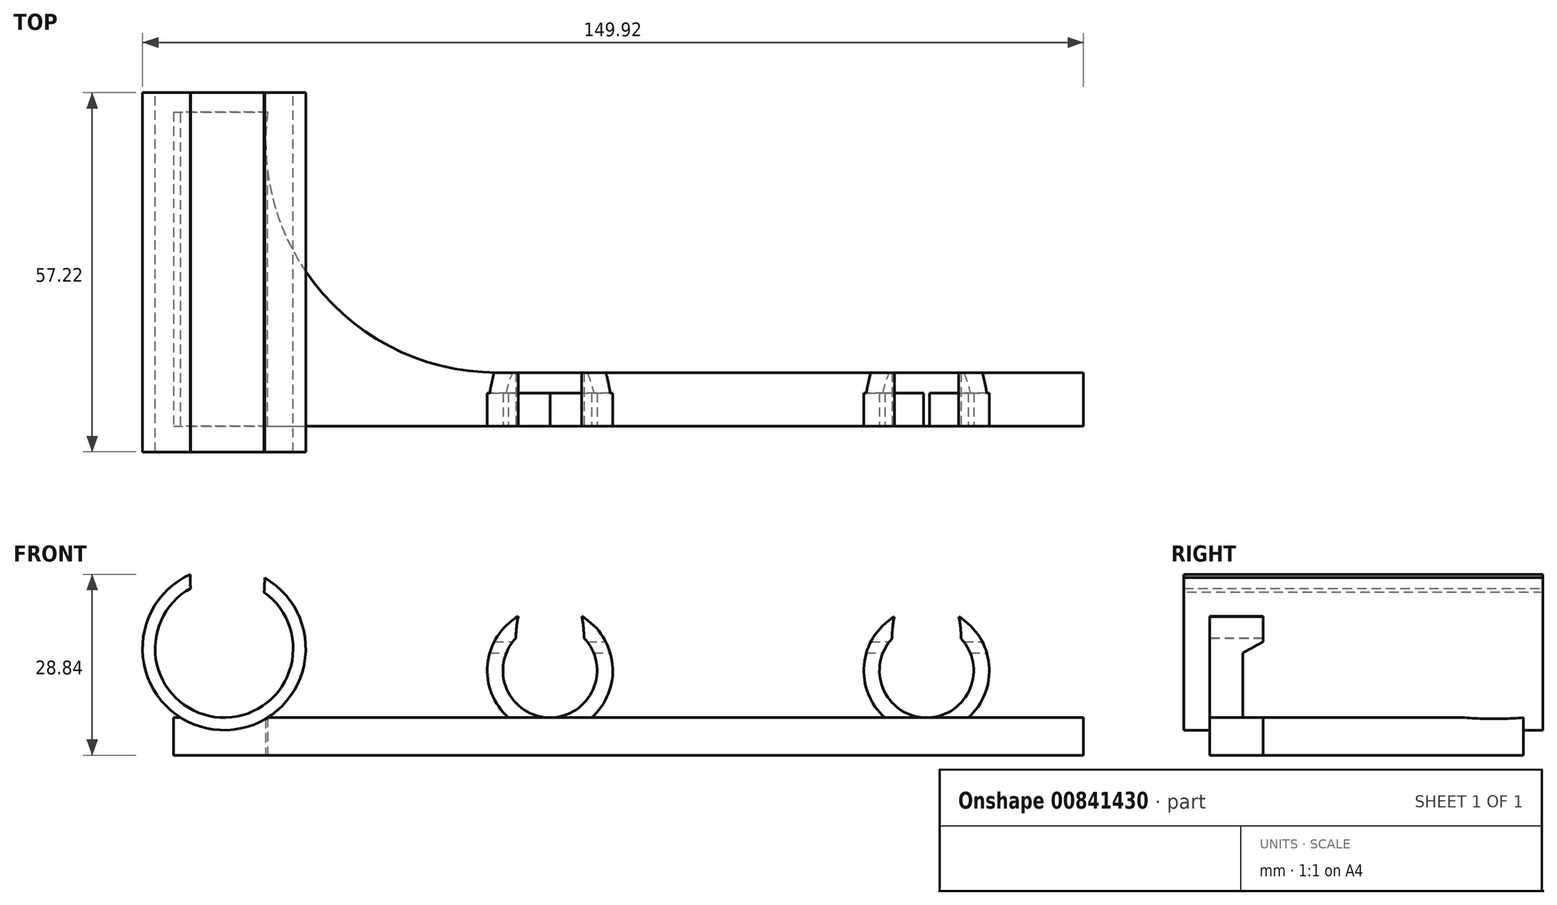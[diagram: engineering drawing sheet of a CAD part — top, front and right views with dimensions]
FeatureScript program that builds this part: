
annotation { "Feature Type Name" : "Feature", "Feature Type Description" : "" }
export const myFeature = defineFeature(function(context is Context, id is Id, definition is map)
    precondition{}
    {
        {
            var Q0;
            Q0=qCreatedBy(makeId("Top.planeOp"),FACE);
            var sketch = newSketch(context, id + "F0", { "sketchPlane" : qUnion([Q0])});
            skLineSegment(sketch, "E0", {"start": v(-14, 18.17) * mm, "end": v(-14, -31.83) * mm});
            skLineSegment(sketch, "E1", {"start": v(-14, -31.83) * mm, "end": v(131, -31.83) * mm});
            skLineSegment(sketch, "E2", {"start": v(131, -31.83) * mm, "end": v(131, -23.3) * mm});
            skLineSegment(sketch, "E3", {"start": v(131, -23.3) * mm, "end": v(37.51, -23.3) * mm});
            skLineSegment(sketch, "E4", {"start": v(-14, 18.17) * mm, "end": v(1, 18.17) * mm});
            skArc(sketch, "E5", {"start": v(1, 18.17) * mm, "mid": v(9.88, -10.82) * mm, "end": v(37.51, -23.3) * mm});
            skSolve(sketch);
        }
        {
            var Q0;
            Q0=makeQuery(id+"F0.imprint","IMPRINT",FACE,{"disambiguationData":[TD([[makeQuery(id+"F0.imprint","IMPRINT",EDGE,{"derivedFrom":sQuery(id+"F0.wireOp",EDGE,"E0")}),1.0]])]});
            extrude(context, id + "F1", {"entities" : qUnion([Q0]), "depth" : 5 * mm, "offsetDistance" : 25 * mm, "hasSecondDirection" : true, "secondDirectionOppositeDirection" : true, "secondDirectionDepth" : 1 * mm});
        }
        {
            var Q0;
            Q0=qCreatedBy(makeId("Front.planeOp"),FACE);
            var sketch = newSketch(context, id + "F2", { "sketchPlane" : qUnion([Q0])});
            skCircle(sketch, "E6", {"center": v(-5.92, 16) * mm, "radius": 11 * mm});
            skCircle(sketch, "E7", {"center": v(-5.92, 16) * mm, "radius": 13 * mm});
            skEllipse(sketch, "E8", {"center": v(-5.38, 26.99) * mm, "majorRadius": 11.85 * mm, "minorRadius": 5.92 * mm, "majorAxis": v(0, 1)});
            skSolve(sketch);
        }
        {
            var Q0;
            {var subQ0=sQuery(id+"F2.wireOp",EDGE,"E8");var subQ1=sQuery(id+"F2.wireOp",EDGE,"E6");var subQ2=makeQuery(id+"F2.imprint","INTERSECT",VERTEX,{"disambiguationData":[OD(0.0)],"derivedFrom":[subQ1,subQ0]});Q0=makeQuery(id+"F2.imprint","IMPRINT",FACE,{"disambiguationData":[TD([[makeQuery(id+"F2.imprint","IMPRINT",EDGE,{"disambiguationData":[TD([[subQ2,-1.0]])],"derivedFrom":subQ1}),-1.0]])]});}
            extrude(context, id + "F3", {"entities" : qUnion([Q0]), "operationType" : NewBodyOperationType.ADD, "depth" : 35.94 * mm, "offsetDistance" : 25 * mm, "hasSecondDirection" : true, "secondDirectionOppositeDirection" : true, "secondDirectionDepth" : 21.28 * mm});
        }
        {
            var Q0;
            Q0=makeQuery(id+"F1.opExtrude","SWEPT_FACE",FACE,{"disambiguationData":[OSD([sQuery(id+"F0.wireOp",EDGE,"E1")])]});
            var sketch = newSketch(context, id + "F4", { "sketchPlane" : qUnion([Q0])});
            skCircle(sketch, "E9", {"center": v(46, 12.5) * mm, "radius": 7.5 * mm});
            skCircle(sketch, "E10", {"center": v(106, 12.49) * mm, "radius": 7.5 * mm});
            skCircle(sketch, "E11", {"center": v(46, 12.5) * mm, "radius": 10 * mm});
            skCircle(sketch, "E12", {"center": v(106, 12.49) * mm, "radius": 10 * mm});
            skEllipse(sketch, "E13", {"center": v(106, 17.49) * mm, "majorRadius": 10 * mm, "minorRadius": 5.5 * mm, "majorAxis": v(0, 1)});
            skEllipse(sketch, "E14", {"center": v(46, 17.5) * mm, "majorRadius": 10 * mm, "minorRadius": 5.43 * mm, "majorAxis": v(0, 1)});
            skSolve(sketch);
        }
        {
            var Q0;
            {var subQ0=sQuery(id+"F4.wireOp",EDGE,"E14");var subQ1=sQuery(id+"F4.wireOp",EDGE,"E9");var subQ2=makeQuery(id+"F4.imprint","INTERSECT",VERTEX,{"disambiguationData":[OD(1.0)],"derivedFrom":[subQ1,subQ0]});Q0=makeQuery(id+"F4.imprint","IMPRINT",FACE,{"disambiguationData":[TD([[makeQuery(id+"F4.imprint","IMPRINT",EDGE,{"disambiguationData":[TD([[subQ2,1.0]])],"derivedFrom":subQ1}),-1.0]])]});}
            var Q1;
            {var subQ0=sQuery(id+"F4.wireOp",EDGE,"E14");var subQ1=sQuery(id+"F4.wireOp",EDGE,"E9");var subQ2=makeQuery(id+"F4.imprint","INTERSECT",VERTEX,{"disambiguationData":[OD(0.0)],"derivedFrom":[subQ1,subQ0]});Q1=makeQuery(id+"F4.imprint","IMPRINT",FACE,{"disambiguationData":[TD([[makeQuery(id+"F4.imprint","IMPRINT",EDGE,{"disambiguationData":[TD([[subQ2,-1.0]])],"derivedFrom":subQ1}),-1.0]])]});}
            var Q2;
            {var subQ0=sQuery(id+"F4.wireOp",EDGE,"E13");var subQ1=sQuery(id+"F4.wireOp",EDGE,"E10");var subQ2=makeQuery(id+"F4.imprint","INTERSECT",VERTEX,{"disambiguationData":[OD(0.0)],"derivedFrom":[subQ1,subQ0]});Q2=makeQuery(id+"F4.imprint","IMPRINT",FACE,{"disambiguationData":[TD([[makeQuery(id+"F4.imprint","IMPRINT",EDGE,{"disambiguationData":[TD([[subQ2,-1.0]])],"derivedFrom":subQ1}),-1.0]])]});}
            var Q3;
            {var subQ0=sQuery(id+"F4.wireOp",EDGE,"E13");var subQ1=sQuery(id+"F4.wireOp",EDGE,"E10");var subQ2=makeQuery(id+"F4.imprint","INTERSECT",VERTEX,{"disambiguationData":[OD(1.0)],"derivedFrom":[subQ1,subQ0]});Q3=makeQuery(id+"F4.imprint","IMPRINT",FACE,{"disambiguationData":[TD([[makeQuery(id+"F4.imprint","IMPRINT",EDGE,{"disambiguationData":[TD([[subQ2,1.0]])],"derivedFrom":subQ1}),-1.0]])]});}
            extrude(context, id + "F5", {"entities" : qUnion([Q0, Q1, Q2, Q3]), "oppositeDirection" : true, "depth" : 8.5 * mm, "offsetDistance" : 25 * mm});
        }
        {
            var Q0;
            Q0=makeQuery(id+"F1.opExtrude","SWEPT_FACE",FACE,{"disambiguationData":[OSD([sQuery(id+"F0.wireOp",EDGE,"E2")])]});
            var sketch = newSketch(context, id + "F6", { "sketchPlane" : qUnion([Q0])});
            skLineSegment(sketch, "E15", {"start": v(-26.55, 5) * mm, "end": v(-26.55, 15.3) * mm});
            skLineSegment(sketch, "E16", {"start": v(-26.55, 15.3) * mm, "end": v(-22.67, 17.44) * mm});
            skLineSegment(sketch, "E17", {"start": v(-22.67, 17.44) * mm, "end": v(-22.67, 5) * mm});
            skLineSegment(sketch, "E18", {"start": v(-22.67, 5) * mm, "end": v(-26.55, 5) * mm});
            skSolve(sketch);
        }
        {
            var Q0;
            {var subQ4=sQuery(id+"F6.wireOp",EDGE,"E15");Q0=makeQuery(id+"F6.imprint","IMPRINT",FACE,{"disambiguationData":[TD([[makeQuery(id+"F6.imprint","IMPRINT",EDGE,{"derivedFrom":subQ4}),-1.0]])]});}
            extrude(context, id + "F7", {"entities" : qUnion([Q0]), "operationType" : NewBodyOperationType.REMOVE, "oppositeDirection" : true, "depth" : 102.26 * mm, "offsetDistance" : 25 * mm});
        }
    });
